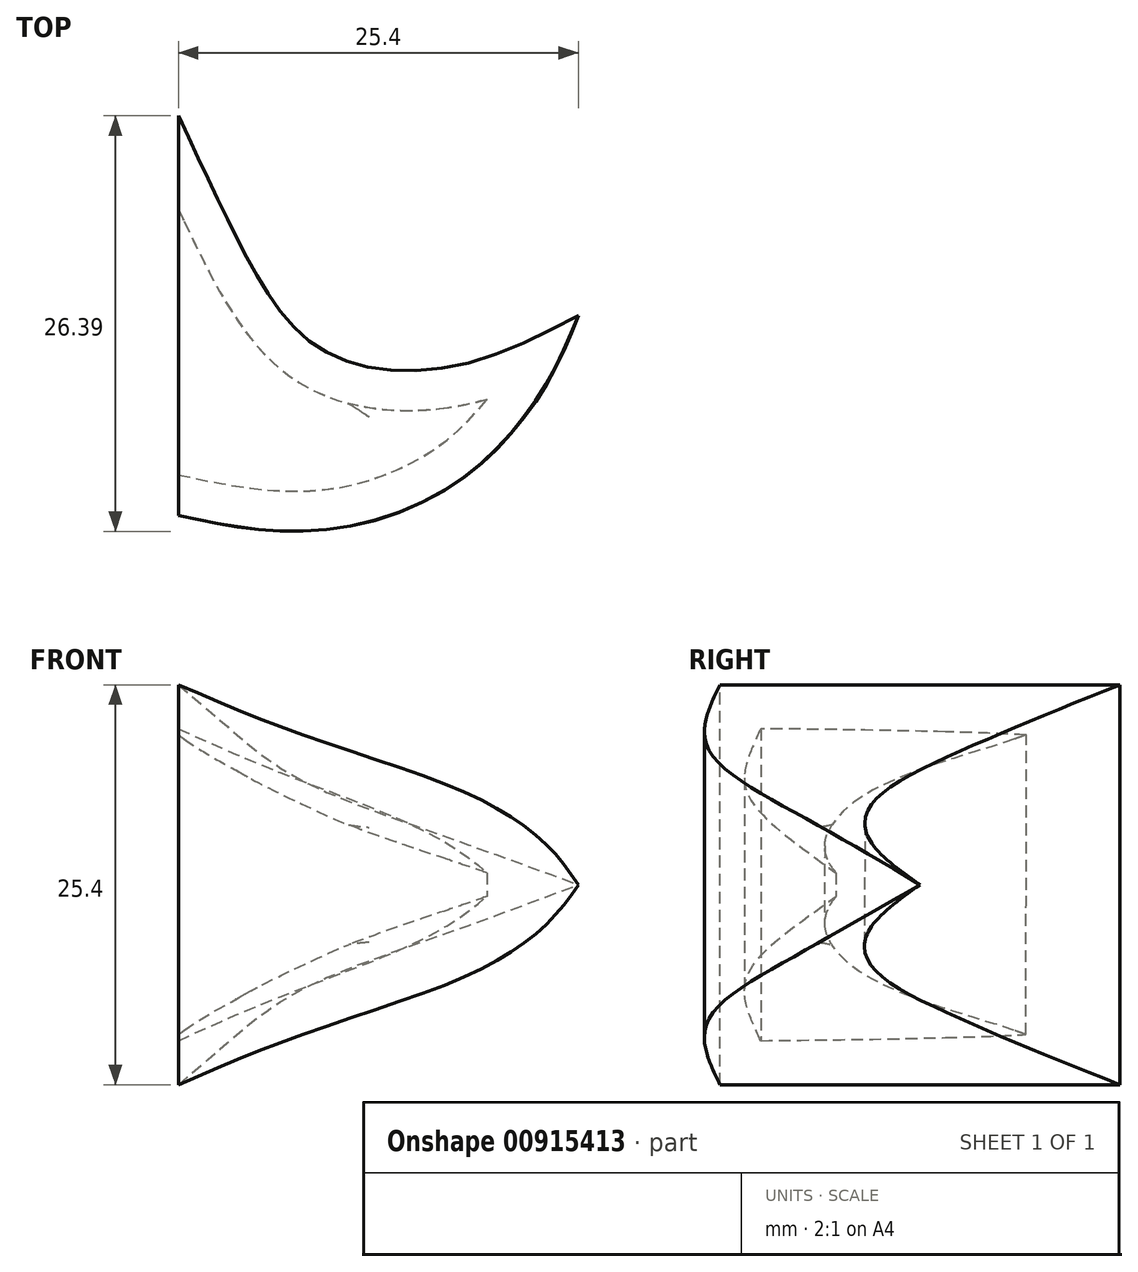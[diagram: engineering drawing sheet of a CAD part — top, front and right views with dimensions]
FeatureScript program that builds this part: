
annotation { "Feature Type Name" : "Feature", "Feature Type Description" : "" }
export const myFeature = defineFeature(function(context is Context, id is Id, definition is map)
    precondition{}
    {
        {
            var Q0;
            Q0=qCreatedBy(makeId("Right.planeOp"),FACE);
            var sketch = newSketch(context, id + "F0", { "sketchPlane" : qUnion([Q0])});
            skLineSegment(sketch, "E0.bottom", {"start": v(12.7, -12.7) * mm, "end": v(-12.7, -12.7) * mm});
            skLineSegment(sketch, "E0.top", {"start": v(12.7, 12.7) * mm, "end": v(-12.7, 12.7) * mm});
            skLineSegment(sketch, "E0.left", {"start": v(12.7, -12.7) * mm, "end": v(12.7, 12.7) * mm});
            skLineSegment(sketch, "E0.right", {"start": v(-12.7, -12.7) * mm, "end": v(-12.7, 12.7) * mm});
            skPoint(sketch, "E0.middle", {"position": v(0, 0) * mm});
            skSolve(sketch);
        }
        {
            var Q0;
            Q0=makeQuery(id+"F0.imprint","IMPRINT",FACE,{"disambiguationData":[TD([[makeQuery(id+"F0.imprint","IMPRINT",EDGE,{"derivedFrom":sQuery(id+"F0.wireOp",EDGE,"E0.bottom")}),-1.0]])]});
            cPlane(context, id + "F1", {"entities" : qUnion([Q0]), "cplaneType" : CPlaneType.OFFSET, "offset" : 25.4 * mm, "width" : 152.4 * mm, "height" : 152.4 * mm});
        }
        {
            var Q0;
            Q0=qCreatedBy(id+"F1.planeOp",FACE);
            var sketch = newSketch(context, id + "F2", { "sketchPlane" : qUnion([Q0])});
            skLineSegment(sketch, "E1", {"start": v(0, 1.8) * mm, "end": v(-1.8, 0) * mm});
            skLineSegment(sketch, "E2", {"start": v(-1.8, 0) * mm, "end": v(0, -1.8) * mm});
            skLineSegment(sketch, "E3", {"start": v(0, -1.8) * mm, "end": v(1.8, 0) * mm});
            skLineSegment(sketch, "E4", {"start": v(1.8, 0) * mm, "end": v(0, 1.8) * mm});
            skLineSegment(sketch, "E5", {"start": v(1.8, 0) * mm, "end": v(-1.8, 0) * mm, "construction": true});
            skLineSegment(sketch, "E6", {"start": v(0, -1.8) * mm, "end": v(0, 1.8) * mm, "construction": true});
            skLineSegment(sketch, "E7", {"start": v(0, -1.8) * mm, "end": v(0, 0) * mm});
            skPoint(sketch, "E7.endSnap0", {"position": v(0, 0) * mm});
            skSolve(sketch);
        }
        {
            var Q0;
            Q0=qCreatedBy(makeId("Top.planeOp"),FACE);
            var sketch = newSketch(context, id + "F3", { "sketchPlane" : qUnion([Q0])});
            skFitSpline(sketch, "E8", {"points": [v(25.4, 0) * mm, v(12.7, -6.35) * mm, v(0, 0) * mm], "startDerivative": vector(-22.94, -23.6) * mm, "endDerivative": vector(-26.77, 24.32) * mm});
            skSolve(sketch);
        }
        {
            var Q0;
            Q0=sQuery(id+"F3.wireOp",EDGE,"E8");
            var Q1;
            Q1=makeQuery(id+"F0.imprint","IMPRINT",FACE,{"disambiguationData":[TD([[makeQuery(id+"F0.imprint","IMPRINT",EDGE,{"derivedFrom":sQuery(id+"F0.wireOp",EDGE,"E0.bottom")}),-1.0]])]});
            var Q2;
            Q2=sQuery(id+"F2.wireOp",VERTEX,"E7.endSnap0");
            loft(context, id + "F4", {"addSections" : true, "spine" : qUnion([Q0]), "sectionCount" : 5, "sheetProfilesArray" : [{ "sheetProfileEntities" : qUnion([Q1]) }, { "sheetProfileEntities" : qUnion([Q2]) }]});
        }
        {
            var Q0;
            Q0=makeQuery(id+"F4.opLoft","CAP_FACE",FACE,{"disambiguationData":[OSD([makeQuery(id+"F0.imprint","IMPRINT",FACE,{"disambiguationData":[TD([[makeQuery(id+"F0.imprint","IMPRINT",EDGE,{"derivedFrom":sQuery(id+"F0.wireOp",EDGE,"E0.bottom")}),-1.0]])]})])],"isStart":true});
            shell(context, id + "F5", {"entities" : qUnion([Q0]), "thickness" : 2.54 * mm});
        }
    });
